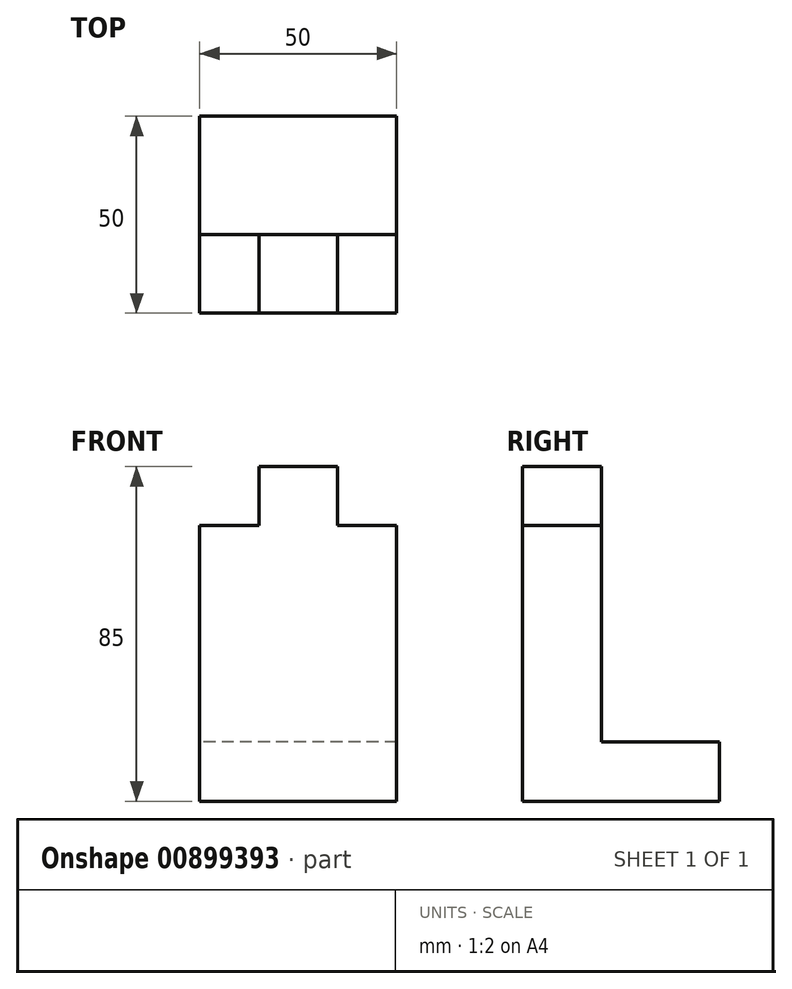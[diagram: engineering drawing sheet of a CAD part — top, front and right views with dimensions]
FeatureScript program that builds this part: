
annotation { "Feature Type Name" : "Feature", "Feature Type Description" : "" }
export const myFeature = defineFeature(function(context is Context, id is Id, definition is map)
    precondition{}
    {
        {
            var Q0;
            Q0=qCreatedBy(makeId("Front.planeOp"),FACE);
            var sketch = newSketch(context, id + "F0", { "sketchPlane" : qUnion([Q0])});
            skLineSegment(sketch, "E0.bottom", {"start": v(0, 0) * mm, "end": v(50, 0) * mm});
            skLineSegment(sketch, "E0.top", {"start": v(0, 70) * mm, "end": v(15, 70) * mm});
            skLineSegment(sketch, "E0.left", {"start": v(0, 0) * mm, "end": v(0, 70) * mm});
            skLineSegment(sketch, "E0.right", {"start": v(50, 0) * mm, "end": v(50, 70) * mm});
            skLineSegment(sketch, "E1", {"start": v(15, 70) * mm, "end": v(15, 85) * mm});
            skLineSegment(sketch, "E2", {"start": v(35, 85) * mm, "end": v(35, 70) * mm});
            skLineSegment(sketch, "E3", {"start": v(15, 85) * mm, "end": v(35, 85) * mm});
            skLineSegment(sketch, "E4.trimOffspring", {"start": v(35, 70) * mm, "end": v(50, 70) * mm});
            skSolve(sketch);
        }
        {
            var Q0;
            Q0 = qSketchRegion(id + "F0", true);
            extrude(context, id + "F1", {"entities" : qUnion([Q0]), "depth" : 20 * mm, "offsetDistance" : 25 * mm});
        }
        {
            var Q0;
            Q0=makeQuery(id+"F1.opExtrude","CAP_FACE",FACE,{"disambiguationData":[OSD([sQuery(id+"F0.wireOp",EDGE,"E0.bottom"),sQuery(id+"F0.wireOp",EDGE,"E0.top"),sQuery(id+"F0.wireOp",EDGE,"E0.left"),sQuery(id+"F0.wireOp",EDGE,"E0.right"),sQuery(id+"F0.wireOp",EDGE,"E1"),sQuery(id+"F0.wireOp",EDGE,"E2"),sQuery(id+"F0.wireOp",EDGE,"E3"),sQuery(id+"F0.wireOp",EDGE,"E4.trimOffspring")])],"isStart":true});
            var sketch = newSketch(context, id + "F2", { "sketchPlane" : qUnion([Q0])});
            skLineSegment(sketch, "E5.bottom", {"start": v(-50, 0) * mm, "end": v(0, 0) * mm});
            skLineSegment(sketch, "E5.top", {"start": v(-50, 15) * mm, "end": v(0, 15) * mm});
            skLineSegment(sketch, "E5.left", {"start": v(-50, 0) * mm, "end": v(-50, 15) * mm});
            skLineSegment(sketch, "E5.right", {"start": v(0, 0) * mm, "end": v(0, 15) * mm});
            skSolve(sketch);
        }
        {
            var Q0;
            Q0 = qSketchRegion(id + "F2", true);
            extrude(context, id + "F3", {"entities" : qUnion([Q0]), "operationType" : NewBodyOperationType.ADD, "depth" : 30 * mm, "offsetDistance" : 25 * mm});
        }
    });
